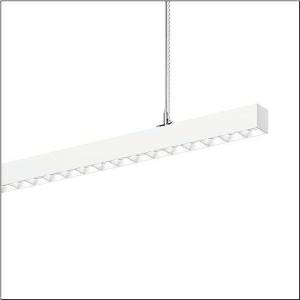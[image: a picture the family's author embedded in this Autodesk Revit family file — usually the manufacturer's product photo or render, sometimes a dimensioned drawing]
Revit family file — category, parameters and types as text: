
# Revit family: silica_21_51mx36da47wb
name_source: partatom
category: Lighting Fixtures
units: mm (PartAtom-declared; Revit-internal decimal feet)

## family parameters
Cut with Voids When Loaded = No
Host = Face
Light Source = No
Part Type = Normal
Room Calculation Point = No
Round Connector Dimension = Use Diameter
Shared = No

## types (1)
- --- (1 x LED, 7060 lm, 40.3 W, 4000K)
    Apparent Load = 40 VA
    CIE Flux Codes = 83 98 100 61 100
    Color Rendering = 80
    Color Temperature = 4000K
    Default Elevation = 1800 mm
    Description = Silica 21, office luminaire, primary light control with darklight reflector, of PMMA, white, CAT 2 (L<= 3000cd/m²), light emission: direct/indirect distribution, primary light characteristic: symmetric, installation type: suspended mounting, LED, rated luminous flux: 7.060lm, luminous efficacy: 175lm/W, light colour: 840, colour temperature: 4000K, control gear: DALI 2, with terminal, 3+2-pole, max. 2.5mm², mains connection: 220..240V, AC, 50/60Hz, rated input power: 40.3W, luminaire housing, of aluminium, traffic white (RAL 9016), length: 1.204mm, width: 53mm, height: 53mm, protection rating (complete): IP20, insulation class (complete): insulation class I (protective earthing), certification: CE, permissible operating ambient temperature: 0..+35°C, standard: EN 50419, packaging unit: 1 piece
    Height = 53 mm
    Lamp = 1 x LED
    Lamp Light Flux = 7060 lm
    Lamp Power = 40.3 W
    Lamp count = 1
    Length = 1204 mm
    Luminous efficacy = 175 lm/W
    Manufacturer = Siteco
    ModVariant = No
    Model = 51MX36DA47WB
    Mounting Place = Ceiling
    Mounting Type = Pendant
    Number of Poles = 1
    OnlyDefault = Yes
    Power Factor = 1
    Product Name = Silica 21
    Product group = office luminaire | ceiling pendant
    ProductGroupID = 903
    Protection Class = Protection class I
    Protection Degree = IP 20
    RLX_Detail_Level = 1
    RLX_Emergency_Light_Flux = 0 lm
    RLX_Emergency_Type = 0
    RLX_Emergency_Type_DB = No
    RlxData = <blob elided: 40873 chars, md5=684c9006>
    Socket = socket
    Standby Power = 0 W
    System Light Flux = 7060 lm
    System Power = 40 W
    Type Comments = factory setting: luminous flux: 100 % | dim-lin: 254 | 336 mA
    Type Image = l_1335921.jpg
    URL = http://relux.com
    VarID = @adj_121563
    Voltage = 0 V
    Weight = 0.00 kg
    Width = 53 mm

## geometry (parser evidence)
native form markers: Blend x4, Sweep x10
no freeform markers — native parametric forms only
